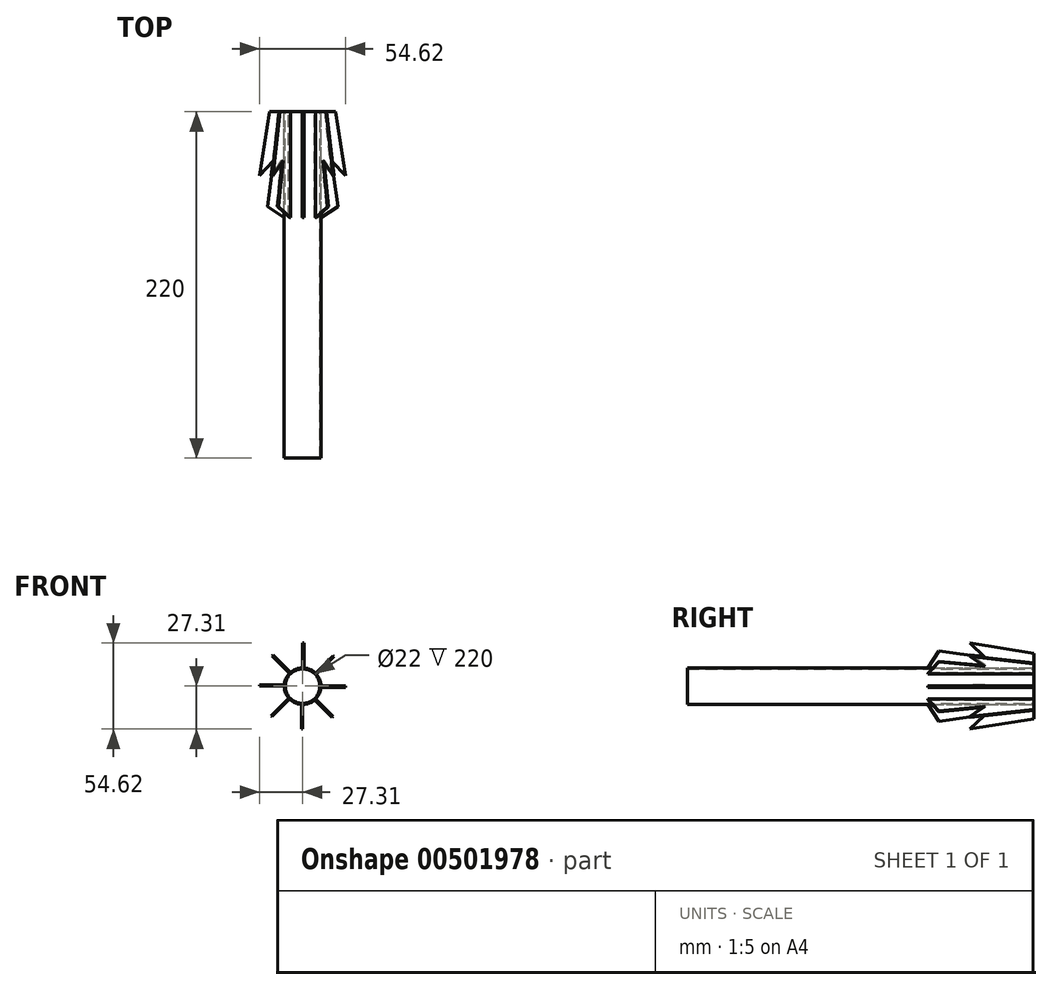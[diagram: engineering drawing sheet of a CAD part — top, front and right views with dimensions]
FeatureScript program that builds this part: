
annotation { "Feature Type Name" : "Feature", "Feature Type Description" : "" }
export const myFeature = defineFeature(function(context is Context, id is Id, definition is map)
    precondition{}
    {
        {
            var Q0;
            Q0=qCreatedBy(makeId("Front.planeOp"),FACE);
            var sketch = newSketch(context, id + "F0", { "sketchPlane" : qUnion([Q0])});
            skCircle(sketch, "E0", {"center": v(0, 0) * mm, "radius": 11 * mm});
            skCircle(sketch, "E1", {"center": v(0, 0) * mm, "radius": 11.65 * mm});
            skSolve(sketch);
        }
        {
            var Q0;
            Q0=makeQuery(id+"F0.imprint","IMPRINT",FACE,{"disambiguationData":[TD([[makeQuery(id+"F0.imprint","IMPRINT",EDGE,{"derivedFrom":sQuery(id+"F0.wireOp",EDGE,"E0")}),-1.0]])]});
            extrude(context, id + "F1", {"entities" : qUnion([Q0]), "depth" : 220 * mm});
        }
        {
            var Q0;
            Q0=qCreatedBy(makeId("Right.planeOp"),FACE);
            var sketch = newSketch(context, id + "F2", { "sketchPlane" : qUnion([Q0])});
            skLineSegment(sketch, "E2", {"start": v(0, 11.36) * mm, "end": v(-67.27, 11.36) * mm});
            skLineSegment(sketch, "E3", {"start": v(-67.27, 11.36) * mm, "end": v(-60.31, 22.38) * mm});
            skLineSegment(sketch, "E4", {"start": v(-60.31, 22.38) * mm, "end": v(-31.02, 18.32) * mm});
            skLineSegment(sketch, "E5", {"start": v(-31.02, 18.32) * mm, "end": v(-40.6, 27.3) * mm});
            skLineSegment(sketch, "E6", {"start": v(-40.6, 27.3) * mm, "end": v(0, 20.93) * mm});
            skLineSegment(sketch, "E7", {"start": v(0, 20.93) * mm, "end": v(0, 11.36) * mm});
            skSolve(sketch);
        }
        {
            var Q0;
            Q0=makeQuery(id+"F2.imprint","IMPRINT",FACE,{"disambiguationData":[TD([[makeQuery(id+"F2.imprint","IMPRINT",EDGE,{"derivedFrom":sQuery(id+"F2.wireOp",EDGE,"E2")}),-1.0]])]});
            extrude(context, id + "F3", {"entities" : qUnion([Q0]), "operationType" : NewBodyOperationType.ADD, "depth" : 0.8 * mm});
        }
        {
            var Q0;
            Q0=makeQuery(id+"F1.opExtrude","SWEPT_BODY",BODY,{"disambiguationData":[OSD([sQuery(id+"F0.wireOp",EDGE,"E0"),sQuery(id+"F0.wireOp",EDGE,"E1")])]});
            var Q1;
            Q1=makeQuery(id+"F1.opExtrude","SWEPT_FACE",FACE,{"disambiguationData":[OSD([sQuery(id+"F0.wireOp",EDGE,"E1")])]});
            circularPattern(context, id + "F4", {"operationType" : NewBodyOperationType.ADD, "entities" : qUnion([Q0]), "axis" : qUnion([Q1]), "angle" : 360 * degree, "instanceCount" : 8, "oppositeDirection" : true, "equalSpace" : true});
        }
    });
